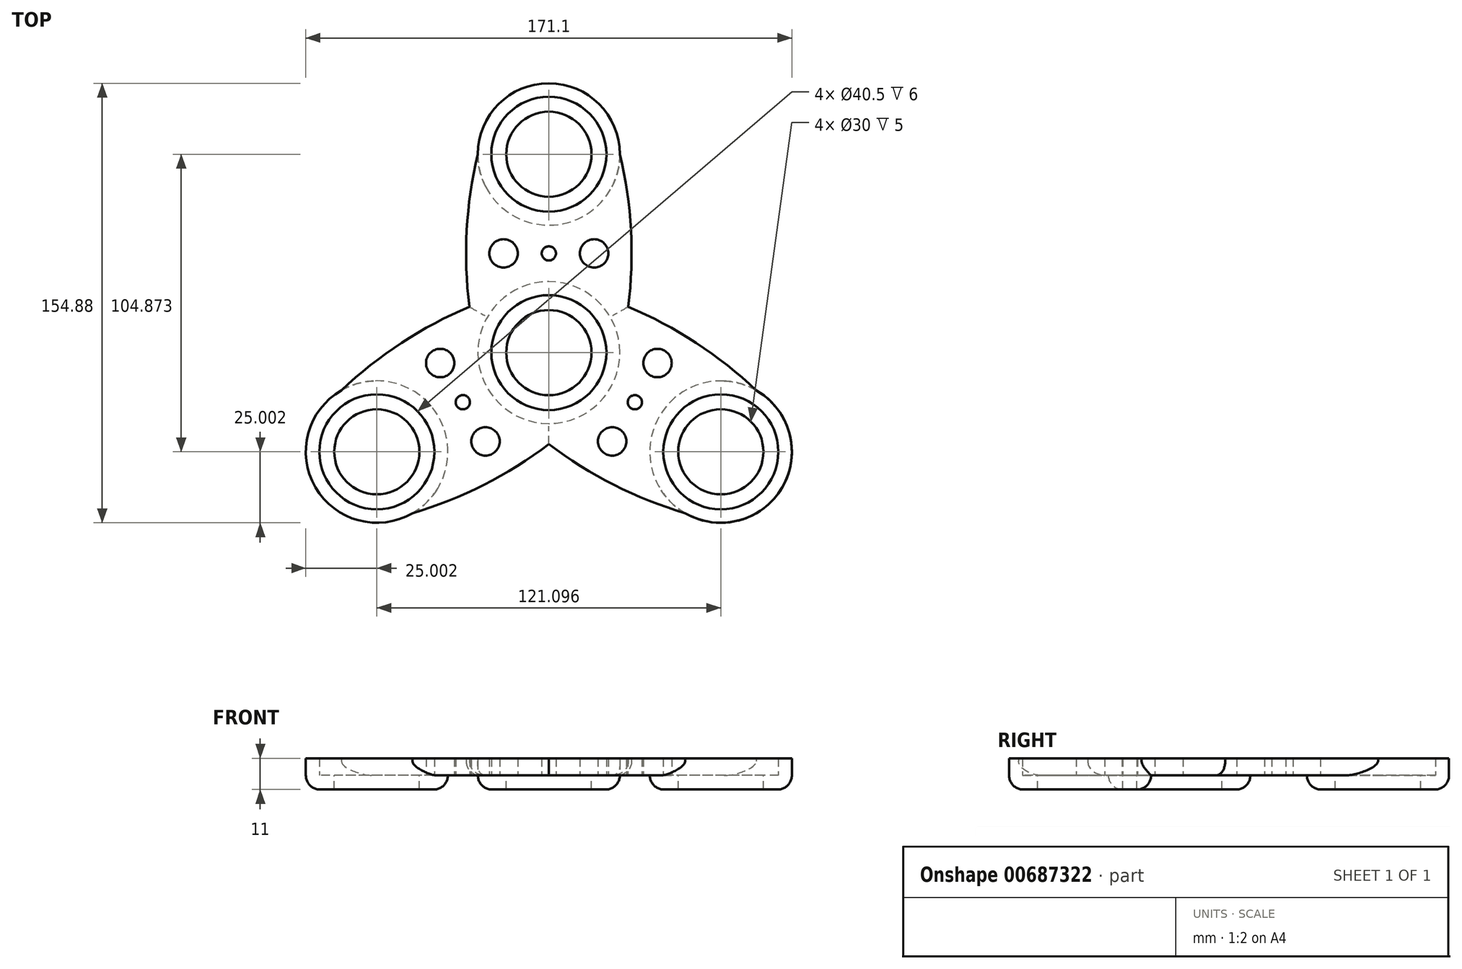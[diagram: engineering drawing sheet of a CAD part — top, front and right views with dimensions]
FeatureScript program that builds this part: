
annotation { "Feature Type Name" : "Feature", "Feature Type Description" : "" }
export const myFeature = defineFeature(function(context is Context, id is Id, definition is map)
    precondition{}
    {
        {
            var Q0;
            Q0=qCreatedBy(makeId("Top.planeOp"),FACE);
            var sketch = newSketch(context, id + "F0", { "sketchPlane" : qUnion([Q0])});
            skCircle(sketch, "E0", {"center": v(0, 0) * mm, "radius": 20.25 * mm});
            skCircle(sketch, "E1", {"center": v(0, 0) * mm, "radius": 15 * mm});
            skLineSegment(sketch, "E2", {"start": v(0, 0) * mm, "end": v(0, 69.92) * mm, "construction": true});
            skCircle(sketch, "E3", {"center": v(0, 69.92) * mm, "radius": 15 * mm});
            skCircle(sketch, "E4", {"center": v(0, 69.92) * mm, "radius": 20.25 * mm});
            skCircle(sketch, "E5", {"center": v(0, 69.92) * mm, "radius": 25 * mm});
            skCircle(sketch, "E6", {"center": v(0, 0) * mm, "radius": 25 * mm});
            skArc(sketch, "E7", {"start": v(-25, 69.92) * mm, "mid": v(-29.13, 34.96) * mm, "end": v(-25, 0) * mm});
            skArc(sketch, "E8", {"start": v(25, 0) * mm, "mid": v(29.13, 34.96) * mm, "end": v(25, 69.92) * mm});
            skArc(sketch, "E9.1.0", {"start": v(-48.05, -56.6) * mm, "mid": v(-15.7, -42.7) * mm, "end": v(12.5, -21.65) * mm});
            skCircle(sketch, "E9.1.1", {"center": v(-60.55, -34.96) * mm, "radius": 25 * mm});
            skCircle(sketch, "E9.1.2", {"center": v(-60.55, -34.96) * mm, "radius": 20.25 * mm});
            skCircle(sketch, "E9.1.3", {"center": v(-60.55, -34.96) * mm, "radius": 15 * mm});
            skArc(sketch, "E9.1.4", {"start": v(-12.5, 21.65) * mm, "mid": v(-44.84, 7.75) * mm, "end": v(-73.05, -13.3) * mm});
            skArc(sketch, "E9.2.0", {"start": v(73.05, -13.3) * mm, "mid": v(44.84, 7.75) * mm, "end": v(12.5, 21.65) * mm});
            skCircle(sketch, "E9.2.1", {"center": v(60.55, -34.96) * mm, "radius": 25 * mm});
            skCircle(sketch, "E9.2.2", {"center": v(60.55, -34.96) * mm, "radius": 20.25 * mm});
            skCircle(sketch, "E9.2.3", {"center": v(60.55, -34.96) * mm, "radius": 15 * mm});
            skArc(sketch, "E9.2.4", {"start": v(-12.5, -21.65) * mm, "mid": v(15.7, -42.7) * mm, "end": v(48.05, -56.6) * mm});
            skLineSegment(sketch, "E10", {"start": v(-25, 69.92) * mm, "end": v(-12.5, 21.65) * mm, "construction": true});
            skCircle(sketch, "E11", {"center": v(-15.95, 34.96) * mm, "radius": 5 * mm});
            skPoint(sketch, "E12", {"position": v(0, 34.96) * mm});
            skLineSegment(sketch, "E13", {"start": v(25, 69.92) * mm, "end": v(12.5, 21.65) * mm, "construction": true});
            skCircle(sketch, "E14", {"center": v(15.95, 34.96) * mm, "radius": 5 * mm});
            skCircle(sketch, "E15.1.0", {"center": v(-22.3, -31.29) * mm, "radius": 5 * mm});
            skCircle(sketch, "E15.1.1", {"center": v(-38.25, -3.67) * mm, "radius": 5 * mm});
            skCircle(sketch, "E15.2.0", {"center": v(38.25, -3.67) * mm, "radius": 5 * mm});
            skCircle(sketch, "E15.2.1", {"center": v(22.3, -31.29) * mm, "radius": 5 * mm});
            skCircle(sketch, "E16", {"center": v(0, 34.96) * mm, "radius": 2.5 * mm});
            skCircle(sketch, "E17.1.0", {"center": v(-30.27, -17.48) * mm, "radius": 2.5 * mm});
            skCircle(sketch, "E17.2.0", {"center": v(30.27, -17.48) * mm, "radius": 2.5 * mm});
            skSolve(sketch);
        }
        {
            var Q0;
            Q0=makeQuery(id+"F0.imprint","IMPRINT",FACE,{"disambiguationData":[TD([[makeQuery(id+"F0.imprint","IMPRINT",EDGE,{"derivedFrom":sQuery(id+"F0.wireOp",EDGE,"E4")}),-1.0]])]});
            var Q1;
            {var subQ0=sQuery(id+"F0.wireOp",EDGE,"E7");var subQ1=sQuery(id+"F0.wireOp",EDGE,"E5");var subQ2=makeQuery(id+"F0.imprint","INTERSECT",VERTEX,{"derivedFrom":[subQ1,subQ0]});Q1=makeQuery(id+"F0.imprint","IMPRINT",FACE,{"disambiguationData":[TD([[makeQuery(id+"F0.imprint","IMPRINT",EDGE,{"disambiguationData":[TD([[subQ2,-1.0]])],"derivedFrom":subQ1}),-1.0]])]});}
            var Q2;
            {var subQ5=sQuery(id+"F0.wireOp",EDGE,"E7");var subQ6=sQuery(id+"F0.wireOp",EDGE,"E6");var subQ7=makeQuery(id+"F0.imprint","INTERSECT",VERTEX,{"derivedFrom":[subQ6,subQ5]});Q2=makeQuery(id+"F0.imprint","IMPRINT",FACE,{"disambiguationData":[TD([[makeQuery(id+"F0.imprint","IMPRINT",EDGE,{"disambiguationData":[TD([[subQ7,-1.0]])],"derivedFrom":subQ6}),-1.0]])]});}
            var Q3;
            {var subQ1=sQuery(id+"F0.wireOp",EDGE,"E6");var subQ8=sQuery(id+"F0.wireOp",EDGE,"E8");var subQ10=makeQuery(id+"F0.imprint","INTERSECT",VERTEX,{"derivedFrom":[subQ1,subQ8]});Q3=makeQuery(id+"F0.imprint","IMPRINT",FACE,{"disambiguationData":[TD([[makeQuery(id+"F0.imprint","IMPRINT",EDGE,{"disambiguationData":[TD([[subQ10,1.0]])],"derivedFrom":subQ1}),-1.0]])]});}
            var Q4;
            Q4=makeQuery(id+"F0.imprint","IMPRINT",FACE,{"disambiguationData":[TD([[makeQuery(id+"F0.imprint","IMPRINT",EDGE,{"derivedFrom":sQuery(id+"F0.wireOp",EDGE,"E0")}),-1.0]])]});
            var Q5;
            {var subQ0=sQuery(id+"F0.wireOp",EDGE,"E7");var subQ1=sQuery(id+"F0.wireOp",EDGE,"E6");var subQ2=makeQuery(id+"F0.imprint","INTERSECT",VERTEX,{"derivedFrom":[subQ1,subQ0]});Q5=makeQuery(id+"F0.imprint","IMPRINT",FACE,{"disambiguationData":[TD([[makeQuery(id+"F0.imprint","IMPRINT",EDGE,{"disambiguationData":[TD([[subQ2,1.0]])],"derivedFrom":subQ1}),-1.0]])]});}
            var Q6;
            {var subQ0=sQuery(id+"F0.wireOp",EDGE,"E9.1.0");var subQ1=sQuery(id+"F0.wireOp",EDGE,"E6");var subQ2=makeQuery(id+"F0.imprint","INTERSECT",VERTEX,{"derivedFrom":[subQ1,subQ0]});Q6=makeQuery(id+"F0.imprint","IMPRINT",FACE,{"disambiguationData":[TD([[makeQuery(id+"F0.imprint","IMPRINT",EDGE,{"disambiguationData":[TD([[subQ2,1.0]])],"derivedFrom":subQ1}),-1.0]])]});}
            var Q7;
            {var subQ0=sQuery(id+"F0.wireOp",EDGE,"E8");var subQ1=sQuery(id+"F0.wireOp",EDGE,"E6");var subQ2=makeQuery(id+"F0.imprint","INTERSECT",VERTEX,{"derivedFrom":[subQ1,subQ0]});Q7=makeQuery(id+"F0.imprint","IMPRINT",FACE,{"disambiguationData":[TD([[makeQuery(id+"F0.imprint","IMPRINT",EDGE,{"disambiguationData":[TD([[subQ2,-1.0]])],"derivedFrom":subQ1}),-1.0]])]});}
            var Q8;
            Q8=makeQuery(id+"F0.imprint","IMPRINT",FACE,{"disambiguationData":[TD([[makeQuery(id+"F0.imprint","IMPRINT",EDGE,{"derivedFrom":sQuery(id+"F0.wireOp",EDGE,"E9.1.2")}),-1.0]])]});
            var Q9;
            Q9=makeQuery(id+"F0.imprint","IMPRINT",FACE,{"disambiguationData":[TD([[makeQuery(id+"F0.imprint","IMPRINT",EDGE,{"derivedFrom":sQuery(id+"F0.wireOp",EDGE,"E9.2.2")}),-1.0]])]});
            extrude(context, id + "F1", {"entities" : qUnion([Q0, Q1, Q2, Q3, Q4, Q5, Q6, Q7, Q8, Q9]), "depth" : 6 * mm, "offsetDistance" : 25 * mm});
        }
        {
            var Q0;
            Q0=makeQuery(id+"F0.imprint","IMPRINT",FACE,{"disambiguationData":[TD([[makeQuery(id+"F0.imprint","IMPRINT",EDGE,{"derivedFrom":sQuery(id+"F0.wireOp",EDGE,"E9.2.2")}),-1.0]])]});
            var Q1;
            Q1=makeQuery(id+"F0.imprint","IMPRINT",FACE,{"disambiguationData":[TD([[makeQuery(id+"F0.imprint","IMPRINT",EDGE,{"derivedFrom":sQuery(id+"F0.wireOp",EDGE,"E9.2.2")}),1.0]])]});
            var Q2;
            Q2=makeQuery(id+"F0.imprint","IMPRINT",FACE,{"disambiguationData":[TD([[makeQuery(id+"F0.imprint","IMPRINT",EDGE,{"derivedFrom":sQuery(id+"F0.wireOp",EDGE,"E0")}),-1.0]])]});
            var Q3;
            Q3=makeQuery(id+"F0.imprint","IMPRINT",FACE,{"disambiguationData":[TD([[makeQuery(id+"F0.imprint","IMPRINT",EDGE,{"derivedFrom":sQuery(id+"F0.wireOp",EDGE,"E0")}),1.0]])]});
            var Q4;
            Q4=makeQuery(id+"F0.imprint","IMPRINT",FACE,{"disambiguationData":[TD([[makeQuery(id+"F0.imprint","IMPRINT",EDGE,{"derivedFrom":sQuery(id+"F0.wireOp",EDGE,"E4")}),-1.0]])]});
            var Q5;
            Q5=makeQuery(id+"F0.imprint","IMPRINT",FACE,{"disambiguationData":[TD([[makeQuery(id+"F0.imprint","IMPRINT",EDGE,{"derivedFrom":sQuery(id+"F0.wireOp",EDGE,"E3")}),-1.0]])]});
            var Q6;
            Q6=makeQuery(id+"F0.imprint","IMPRINT",FACE,{"disambiguationData":[TD([[makeQuery(id+"F0.imprint","IMPRINT",EDGE,{"derivedFrom":sQuery(id+"F0.wireOp",EDGE,"E9.1.2")}),-1.0]])]});
            var Q7;
            Q7=makeQuery(id+"F0.imprint","IMPRINT",FACE,{"disambiguationData":[TD([[makeQuery(id+"F0.imprint","IMPRINT",EDGE,{"derivedFrom":sQuery(id+"F0.wireOp",EDGE,"E9.1.2")}),1.0]])]});
            extrude(context, id + "F2", {"entities" : qUnion([Q0, Q1, Q2, Q3, Q4, Q5, Q6, Q7]), "operationType" : NewBodyOperationType.ADD, "oppositeDirection" : true, "depth" : 5 * mm, "offsetDistance" : 25 * mm});
        }
        {
            var Q0;
            Q0=makeQuery(id+"F2.opExtrude","CAP_EDGE",EDGE,{"disambiguationData":[OSD([sQuery(id+"F0.wireOp",EDGE,"E9.1.1")])],"isStart":false});
            var Q1;
            Q1=makeQuery(id+"F2.opExtrude","CAP_EDGE",EDGE,{"disambiguationData":[OSD([sQuery(id+"F0.wireOp",EDGE,"E9.2.1")])],"isStart":false});
            var Q2;
            Q2=makeQuery(id+"F2.opExtrude","CAP_EDGE",EDGE,{"disambiguationData":[OSD([sQuery(id+"F0.wireOp",EDGE,"E6")])],"isStart":false});
            var Q3;
            Q3=makeQuery(id+"F2.opExtrude","CAP_EDGE",EDGE,{"disambiguationData":[OSD([sQuery(id+"F0.wireOp",EDGE,"E5")])],"isStart":false});
            var Q4;
            Q4=makeQuery(id+"F1.opExtrude","CAP_EDGE",EDGE,{"disambiguationData":[OSD([sQuery(id+"F0.wireOp",EDGE,"E9.1.4")])],"isStart":true});
            var Q5;
            Q5=makeQuery(id+"F1.opExtrude","CAP_EDGE",EDGE,{"disambiguationData":[OSD([sQuery(id+"F0.wireOp",EDGE,"E7")])],"isStart":true});
            var Q6;
            Q6=makeQuery(id+"F1.opExtrude","CAP_EDGE",EDGE,{"disambiguationData":[OSD([sQuery(id+"F0.wireOp",EDGE,"E8")])],"isStart":true});
            var Q7;
            Q7=makeQuery(id+"F1.opExtrude","CAP_EDGE",EDGE,{"disambiguationData":[OSD([sQuery(id+"F0.wireOp",EDGE,"E9.2.0")])],"isStart":true});
            var Q8;
            Q8=makeQuery(id+"F1.opExtrude","CAP_EDGE",EDGE,{"disambiguationData":[OSD([sQuery(id+"F0.wireOp",EDGE,"E9.1.0")])],"isStart":true});
            var Q9;
            Q9=makeQuery(id+"F1.opExtrude","CAP_EDGE",EDGE,{"disambiguationData":[OSD([sQuery(id+"F0.wireOp",EDGE,"E9.2.4")])],"isStart":true});
            fillet(context, id + "F3", {"entities" : qUnion([Q0, Q1, Q2, Q3, Q4, Q5, Q6, Q7, Q8, Q9]), "radius" : 5 * mm, "tangentPropagation" : true, "allowEdgeOverflow" : false});
        }
    });
